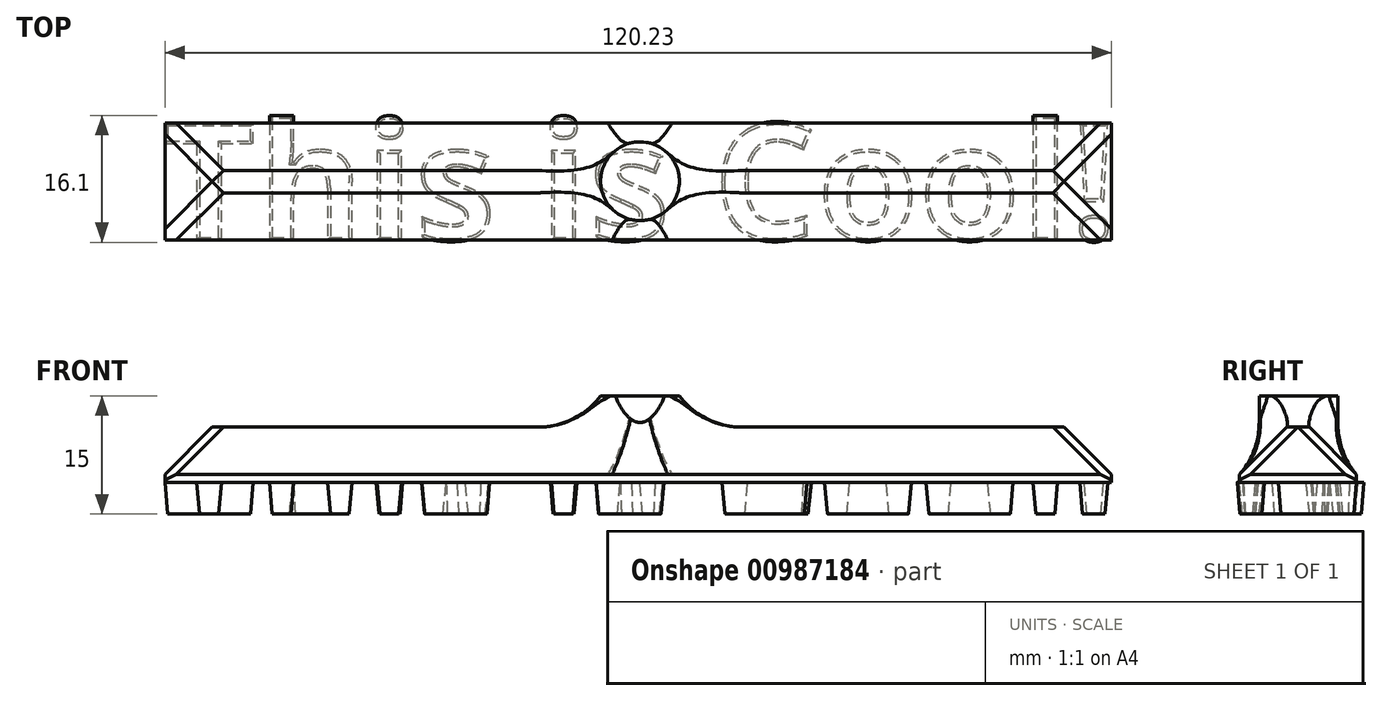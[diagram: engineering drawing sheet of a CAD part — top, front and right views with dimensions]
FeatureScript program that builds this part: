
annotation { "Feature Type Name" : "Feature", "Feature Type Description" : "" }
export const myFeature = defineFeature(function(context is Context, id is Id, definition is map)
    precondition{}
    {
        {
            var Q0;
            Q0=qCreatedBy(makeId("Top.planeOp"),FACE);
            var sketch = newSketch(context, id + "F0", { "sketchPlane" : qUnion([Q0])});
            skText(sketch, "E0", { "text": "This is Cool!", "fontName": "OpenSans-Bold.ttf"});
            const initialGuessF0  = {"E0": [-0.06077, -0.0075, 1, 0, 0.015]};
            skSetInitialGuess(sketch, initialGuessF0);
            skSolve(sketch);
        }
        {
            var Q0;
            Q0 = qSketchRegion(id + "F0", true);
            var Q1;
            Q1 = qSketchRegion(id + "F2", true);
            extrude(context, id + "F1", {"entities" : qUnion([Q0, Q1]), "oppositeDirection" : true, "depth" : 4 * mm, "offsetDistance" : 25 * mm, "hasDraft" : true, "draftAngle" : 5 * degree, "draftPullDirection" : true});
        }
        {
            var Q0;
            Q0=makeQuery(id+"F1.opExtrude","CAP_FACE",FACE,{"disambiguationData":[OSD([sQuery(id+"F0.wireOp",EDGE,"E0.sketch_text.stroke-0"),sQuery(id+"F0.wireOp",EDGE,"E0.sketch_text.stroke-1"),sQuery(id+"F0.wireOp",EDGE,"E0.sketch_text.stroke-2"),sQuery(id+"F0.wireOp",EDGE,"E0.sketch_text.stroke-3"),sQuery(id+"F0.wireOp",EDGE,"E0.sketch_text.stroke-4"),sQuery(id+"F0.wireOp",EDGE,"E0.sketch_text.stroke-5"),sQuery(id+"F0.wireOp",EDGE,"E0.sketch_text.stroke-6"),sQuery(id+"F0.wireOp",EDGE,"E0.sketch_text.stroke-7")])],"isStart":true});
            var sketch = newSketch(context, id + "F2", { "sketchPlane" : qUnion([Q0])});
            skLineSegment(sketch, "E1.bottom", {"start": v(-60.35, 7.37) * mm, "end": v(59.88, 7.37) * mm});
            skLineSegment(sketch, "E1.top", {"start": v(-60.35, -7.5) * mm, "end": v(59.88, -7.5) * mm});
            skLineSegment(sketch, "E1.left", {"start": v(-60.35, 7.37) * mm, "end": v(-60.35, -7.5) * mm});
            skLineSegment(sketch, "E1.right", {"start": v(59.88, 7.37) * mm, "end": v(59.88, -7.5) * mm});
            skSolve(sketch);
        }
        {
            var Q0;
            {var subQ2=sQuery(id+"F2.wireOp",EDGE,"E1.top");Q0=makeQuery(id+"F2.imprint","IMPRINT",FACE,{"disambiguationData":[TD([[makeQuery(id+"F2.imprint","IMPRINT",EDGE,{"derivedFrom":subQ2}),1.0]])]});}
            var Q1;
            Q1=makeQuery(id+"F2.imprint","IMPRINT",FACE,{"disambiguationData":[TD([[makeQuery(id+"F2.imprint","IMPRINT",EDGE,{"derivedFrom":makeQuery(id+"F1.opExtrude","CAP_EDGE",EDGE,{"disambiguationData":[OSD([sQuery(id+"F0.wireOp",EDGE,"E0.sketch_text.stroke-0")])],"isStart":false})}),-1.0]])]});
            var Q2;
            {var subQ0=sQuery(id+"F2.wireOp",EDGE,"E1.right");Q2=makeQuery(id+"F2.imprint","IMPRINT",FACE,{"disambiguationData":[TD([[makeQuery(id+"F2.imprint","IMPRINT",EDGE,{"derivedFrom":subQ0}),-1.0]])]});}
            var Q3;
            {var subQ0=makeQuery(id+"F1.opExtrude","CAP_EDGE",EDGE,{"disambiguationData":[OSD([sQuery(id+"F0.wireOp",EDGE,"E0.sketch_text.stroke-1")])],"isStart":true});Q3=makeQuery(id+"F2.imprint","IMPRINT",FACE,{"disambiguationData":[TD([[makeQuery(id+"F2.imprint","IMPRINT",EDGE,{"derivedFrom":subQ0}),-1.0]])]});}
            extrude(context, id + "F3", {"entities" : qUnion([Q0, Q1, Q2, Q3]), "operationType" : NewBodyOperationType.ADD, "depth" : 1 * mm, "offsetDistance" : 25 * mm});
        }
        {
            var Q0;
            Q0=makeQuery(id+"F3.opExtrude","CAP_FACE",FACE,{"disambiguationData":[OSD([sQuery(id+"F2.wireOp",EDGE,"E1.bottom"),sQuery(id+"F2.wireOp",EDGE,"E1.top"),sQuery(id+"F2.wireOp",EDGE,"E1.left"),sQuery(id+"F2.wireOp",EDGE,"E1.right")])],"isStart":false});
            var sketch = newSketch(context, id + "F4", { "sketchPlane" : qUnion([Q0])});
            skCircle(sketch, "E2", {"center": v(0, 0) * mm, "radius": 5 * mm});
            skSolve(sketch);
        }
        {
            var Q0;
            Q0 = qSketchRegion(id + "F4", true);
            extrude(context, id + "F5", {"entities" : qUnion([Q0]), "depth" : 10 * mm, "offsetDistance" : 25 * mm});
        }
        {
            var Q0;
            Q0=makeQuery(id+"F3.opExtrude","CAP_FACE",FACE,{"disambiguationData":[OSD([sQuery(id+"F2.wireOp",EDGE,"E1.bottom"),sQuery(id+"F2.wireOp",EDGE,"E1.top"),sQuery(id+"F2.wireOp",EDGE,"E1.left"),sQuery(id+"F2.wireOp",EDGE,"E1.right")])],"isStart":false});
            extrude(context, id + "F6", {"entities" : qUnion([Q0]), "operationType" : NewBodyOperationType.ADD, "depth" : 14 * mm, "offsetDistance" : 25 * mm, "hasDraft" : true, "draftAngle" : 45 * degree, "draftPullDirection" : true});
        }
        {
            var Q0;
            {var subQ0=makeQuery(id+"F6.opExtrude","SWEPT_FACE",FACE,{"disambiguationData":[OSD([sQuery(id+"F2.wireOp",EDGE,"E1.bottom")])]});var subQ1=makeQuery(id+"F6.opExtrude","SWEPT_FACE",FACE,{"disambiguationData":[OSD([sQuery(id+"F2.wireOp",EDGE,"E1.top")])]});Q0=makeQuery(id+"F6.boolean.opBoolean","SPLIT",EDGE,{"disambiguationData":[TD([makeQuery(id+"F6.opExtrude","SWEPT_FACE",FACE,{"disambiguationData":[OSD([sQuery(id+"F2.wireOp",EDGE,"E1.left")])]})])],"derivedFrom":makeQuery(id+"F6.*.draft.opDraft","TWEAK_EDGE",EDGE,{"derivedFrom":[subQ0,subQ1]})});}
            var Q1;
            {var subQ0=makeQuery(id+"F6.opExtrude","SWEPT_FACE",FACE,{"disambiguationData":[OSD([sQuery(id+"F2.wireOp",EDGE,"E1.bottom")])]});var subQ1=makeQuery(id+"F6.opExtrude","SWEPT_FACE",FACE,{"disambiguationData":[OSD([sQuery(id+"F2.wireOp",EDGE,"E1.top")])]});Q1=makeQuery(id+"F6.boolean.opBoolean","SPLIT",EDGE,{"disambiguationData":[TD([makeQuery(id+"F6.opExtrude","SWEPT_FACE",FACE,{"disambiguationData":[OSD([sQuery(id+"F2.wireOp",EDGE,"E1.right")])]})])],"derivedFrom":makeQuery(id+"F6.*.draft.opDraft","TWEAK_EDGE",EDGE,{"derivedFrom":[subQ0,subQ1]})});}
            var Q2;
            Q2=makeQuery(id+"F6.opExtrude","SWEPT_EDGE",EDGE,{"disambiguationData":[OSD([sQuery(id+"F2.wireOp",EDGE,"E1.bottom"),sQuery(id+"F2.wireOp",EDGE,"E1.right")])]});
            var Q3;
            Q3=makeQuery(id+"F6.opExtrude","SWEPT_EDGE",EDGE,{"disambiguationData":[OSD([sQuery(id+"F2.wireOp",EDGE,"E1.top"),sQuery(id+"F2.wireOp",EDGE,"E1.right")])]});
            var Q4;
            Q4=makeQuery(id+"F6.opExtrude","SWEPT_EDGE",EDGE,{"disambiguationData":[OSD([sQuery(id+"F2.wireOp",EDGE,"E1.top"),sQuery(id+"F2.wireOp",EDGE,"E1.left")])]});
            var Q5;
            Q5=makeQuery(id+"F6.opExtrude","SWEPT_EDGE",EDGE,{"disambiguationData":[OSD([sQuery(id+"F2.wireOp",EDGE,"E1.bottom"),sQuery(id+"F2.wireOp",EDGE,"E1.left")])]});
            chamfer(context, id + "F7", {"entities" : qUnion([Q0, Q1, Q2, Q3, Q4, Q5]), "width" : 2 * mm, "tangentPropagation" : true});
        }
        {
            var Q0;
            {var subQ0=makeQuery(id+"F5.opExtrude","SWEPT_FACE",FACE,{"disambiguationData":[OSD([sQuery(id+"F4.wireOp",EDGE,"E2")])]});var subQ1=makeQuery(id+"F6.opExtrude","SWEPT_FACE",FACE,{"disambiguationData":[OSD([sQuery(id+"F2.wireOp",EDGE,"E1.bottom")])]});var subQ2=makeQuery(id+"F6.opExtrude","SWEPT_FACE",FACE,{"disambiguationData":[OSD([sQuery(id+"F2.wireOp",EDGE,"E1.top")])]});Q0=makeQuery(id+"F7.opChamfer","BLEND_EDGE",EDGE,{"blendedFrom":[makeQuery(id+"F6.boolean.opBoolean","SPLIT",EDGE,{"disambiguationData":[TD([makeQuery(id+"F6.opExtrude","SWEPT_FACE",FACE,{"disambiguationData":[OSD([sQuery(id+"F2.wireOp",EDGE,"E1.left")])]})])],"derivedFrom":makeQuery(id+"F6.*.draft.opDraft","TWEAK_EDGE",EDGE,{"derivedFrom":[subQ1,subQ2]})}),subQ0],"blendedInto":[subQ0]});}
            var Q1;
            Q1=makeQuery(id+"F6.boolean.opBoolean","INTERSECT",EDGE,{"derivedFrom":[makeQuery(id+"F5.opExtrude","SWEPT_FACE",FACE,{"disambiguationData":[OSD([sQuery(id+"F4.wireOp",EDGE,"E2")])]}),makeQuery(id+"F6.opExtrude","SWEPT_FACE",FACE,{"disambiguationData":[OSD([sQuery(id+"F2.wireOp",EDGE,"E1.top")])]})]});
            var Q2;
            {var subQ0=makeQuery(id+"F5.opExtrude","SWEPT_FACE",FACE,{"disambiguationData":[OSD([sQuery(id+"F4.wireOp",EDGE,"E2")])]});var subQ1=makeQuery(id+"F6.opExtrude","SWEPT_FACE",FACE,{"disambiguationData":[OSD([sQuery(id+"F2.wireOp",EDGE,"E1.bottom")])]});var subQ2=makeQuery(id+"F6.opExtrude","SWEPT_FACE",FACE,{"disambiguationData":[OSD([sQuery(id+"F2.wireOp",EDGE,"E1.top")])]});Q2=makeQuery(id+"F7.opChamfer","BLEND_EDGE",EDGE,{"blendedFrom":[makeQuery(id+"F6.boolean.opBoolean","SPLIT",EDGE,{"disambiguationData":[TD([makeQuery(id+"F6.opExtrude","SWEPT_FACE",FACE,{"disambiguationData":[OSD([sQuery(id+"F2.wireOp",EDGE,"E1.right")])]})])],"derivedFrom":makeQuery(id+"F6.*.draft.opDraft","TWEAK_EDGE",EDGE,{"derivedFrom":[subQ1,subQ2]})}),subQ0],"blendedInto":[subQ0]});}
            var Q3;
            Q3=makeQuery(id+"F6.boolean.opBoolean","INTERSECT",EDGE,{"derivedFrom":[makeQuery(id+"F5.opExtrude","SWEPT_FACE",FACE,{"disambiguationData":[OSD([sQuery(id+"F4.wireOp",EDGE,"E2")])]}),makeQuery(id+"F6.opExtrude","SWEPT_FACE",FACE,{"disambiguationData":[OSD([sQuery(id+"F2.wireOp",EDGE,"E1.bottom")])]})]});
            fillet(context, id + "F8", {"entities" : qUnion([Q0, Q1, Q2, Q3]), "radius" : 10 * mm, "tangentPropagation" : true, "allowEdgeOverflow" : false});
        }
    });
